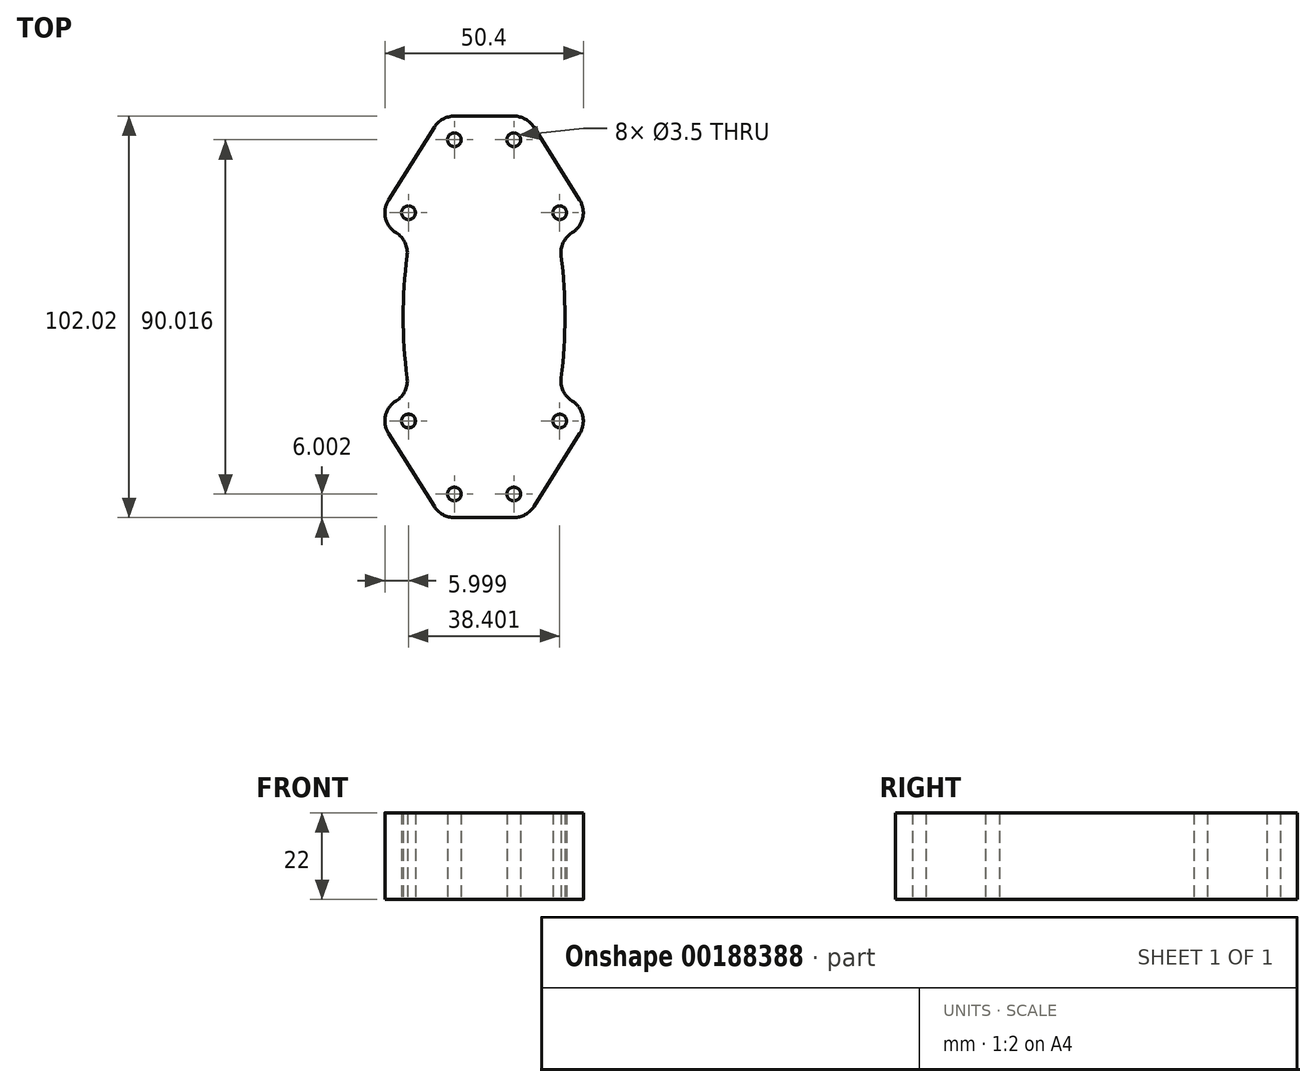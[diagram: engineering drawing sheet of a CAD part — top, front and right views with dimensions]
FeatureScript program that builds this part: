
annotation { "Feature Type Name" : "Feature", "Feature Type Description" : "" }
export const myFeature = defineFeature(function(context is Context, id is Id, definition is map)
    precondition{}
    {
        {
            var Q0;
            Q0=qCreatedBy(makeId("Top.planeOp"),FACE);
            var sketch = newSketch(context, id + "F0", { "sketchPlane" : qUnion([Q0])});
            skLineSegment(sketch, "E0.bottom", {"start": v(18, 18) * mm, "end": v(-18, 18) * mm});
            skLineSegment(sketch, "E0.top", {"start": v(18, -18) * mm, "end": v(-18, -18) * mm});
            skLineSegment(sketch, "E0.left", {"start": v(18, 18) * mm, "end": v(18, -18) * mm});
            skLineSegment(sketch, "E0.right", {"start": v(-18, 18) * mm, "end": v(-18, -18) * mm});
            skPoint(sketch, "E0.middle", {"position": v(0, 0) * mm});
            skLineSegment(sketch, "E1.bottom", {"start": v(15.25, 15.25) * mm, "end": v(-15.25, 15.25) * mm, "construction": true});
            skLineSegment(sketch, "E1.top", {"start": v(15.25, -15.25) * mm, "end": v(-15.25, -15.25) * mm, "construction": true});
            skLineSegment(sketch, "E1.left", {"start": v(15.25, 15.25) * mm, "end": v(15.25, -15.25) * mm, "construction": true});
            skLineSegment(sketch, "E1.right", {"start": v(-15.25, 15.25) * mm, "end": v(-15.25, -15.25) * mm, "construction": true});
            skCircle(sketch, "E2", {"center": v(-15.25, 15.25) * mm, "radius": 1.7 * mm});
            skCircle(sketch, "E3", {"center": v(15.25, 15.25) * mm, "radius": 1.7 * mm});
            skCircle(sketch, "E4", {"center": v(15.25, -15.25) * mm, "radius": 1.7 * mm});
            skCircle(sketch, "E5", {"center": v(-15.25, -15.25) * mm, "radius": 1.7 * mm});
            skLineSegment(sketch, "E6", {"start": v(-73.5, 0) * mm, "end": v(73.5, 0) * mm, "construction": true});
            skLineSegment(sketch, "E7", {"start": v(0, 73.5) * mm, "end": v(0, -73.5) * mm, "construction": true});
            skCircle(sketch, "E8", {"center": v(-73.5, 73.5) * mm, "radius": 63.5 * mm, "construction": true});
            skCircle(sketch, "E9.MirrorC", {"center": v(-73.5, -73.5) * mm, "radius": 63.5 * mm, "construction": true});
            skCircle(sketch, "E10.MirrorC", {"center": v(73.5, 73.5) * mm, "radius": 63.5 * mm, "construction": true});
            skCircle(sketch, "E11.MirrorC", {"center": v(73.5, -73.5) * mm, "radius": 63.5 * mm, "construction": true});
            skLineSegment(sketch, "E12", {"start": v(-73.5, 10) * mm, "end": v(-73.5, -10) * mm, "construction": true});
            skCircle(sketch, "E13", {"center": v(-73.5, -73.5) * mm, "radius": 15 * mm, "construction": true});
            skLineSegment(sketch, "E14.bottom", {"start": v(-56.54, -72.3) * mm, "end": v(-1.5, -37.72) * mm, "construction": true});
            skLineSegment(sketch, "E14.top", {"start": v(-65.05, -58.75) * mm, "end": v(-10.01, -24.17) * mm, "construction": true});
            skLineSegment(sketch, "E14.left", {"start": v(-56.54, -72.3) * mm, "end": v(-65.05, -58.75) * mm, "construction": true});
            skLineSegment(sketch, "E14.right", {"start": v(-1.5, -37.72) * mm, "end": v(-10.01, -24.17) * mm, "construction": true});
            skLineSegment(sketch, "E15", {"start": v(-73.5, -73.5) * mm, "end": v(-5.76, -30.95) * mm, "construction": true});
            skLineSegment(sketch, "E16.MirrorCS", {"start": v(1.5, -37.72) * mm, "end": v(10.01, -24.17) * mm, "construction": true});
            skLineSegment(sketch, "E17.MirrorCS", {"start": v(65.05, -58.75) * mm, "end": v(10.01, -24.17) * mm, "construction": true});
            skCircle(sketch, "E18.MirrorC", {"center": v(73.5, -73.5) * mm, "radius": 15 * mm, "construction": true});
            skLineSegment(sketch, "E19.MirrorCS", {"start": v(56.54, -72.3) * mm, "end": v(65.05, -58.75) * mm, "construction": true});
            skLineSegment(sketch, "E20.MirrorCS", {"start": v(56.54, -72.3) * mm, "end": v(1.5, -37.72) * mm, "construction": true});
            skLineSegment(sketch, "E21.MirrorCS", {"start": v(-1.5, 37.72) * mm, "end": v(-10.01, 24.17) * mm, "construction": true});
            skCircle(sketch, "E22.MirrorC", {"center": v(-73.5, 73.5) * mm, "radius": 15 * mm, "construction": true});
            skLineSegment(sketch, "E23.MirrorCS", {"start": v(-56.54, 72.3) * mm, "end": v(-65.05, 58.75) * mm, "construction": true});
            skLineSegment(sketch, "E24.MirrorCS", {"start": v(-65.05, 58.75) * mm, "end": v(-10.01, 24.17) * mm, "construction": true});
            skLineSegment(sketch, "E25.MirrorCS", {"start": v(-56.54, 72.3) * mm, "end": v(-1.5, 37.72) * mm, "construction": true});
            skCircle(sketch, "E26.MirrorC", {"center": v(73.5, 73.5) * mm, "radius": 15 * mm, "construction": true});
            skLineSegment(sketch, "E27.MirrorCS", {"start": v(56.54, 72.3) * mm, "end": v(65.05, 58.75) * mm, "construction": true});
            skLineSegment(sketch, "E28.MirrorCS", {"start": v(65.05, 58.75) * mm, "end": v(10.01, 24.17) * mm, "construction": true});
            skLineSegment(sketch, "E29.MirrorCS", {"start": v(1.5, 37.72) * mm, "end": v(10.01, 24.17) * mm, "construction": true});
            skLineSegment(sketch, "E30.MirrorCS", {"start": v(56.54, 72.3) * mm, "end": v(1.5, 37.72) * mm, "construction": true});
            skCircle(sketch, "E31", {"center": v(-73.5, -73.5) * mm, "radius": 65 * mm, "construction": true});
            skLineSegment(sketch, "E32.bottom", {"start": v(19.5, 44.5) * mm, "end": v(-19.5, 44.5) * mm, "construction": true});
            skLineSegment(sketch, "E32.top", {"start": v(19.5, -44.5) * mm, "end": v(-19.5, -44.5) * mm, "construction": true});
            skLineSegment(sketch, "E32.left", {"start": v(19.5, 44.5) * mm, "end": v(19.5, -44.5) * mm, "construction": true});
            skLineSegment(sketch, "E32.right", {"start": v(-19.5, 44.5) * mm, "end": v(-19.5, -44.5) * mm, "construction": true});
            skLineSegment(sketch, "E33", {"start": v(5.76, 30.95) * mm, "end": v(60.8, 65.52) * mm, "construction": true});
            skLineSegment(sketch, "E34", {"start": v(-10, -73.5) * mm, "end": v(10, -73.5) * mm, "construction": true});
            skLineSegment(sketch, "E35", {"start": v(-73.5, -73.5) * mm, "end": v(-73.5, 73.5) * mm, "construction": true});
            skLineSegment(sketch, "E36", {"start": v(-73.5, -73.5) * mm, "end": v(73.5, -73.5) * mm, "construction": true});
            skLineSegment(sketch, "E37", {"start": v(18, -18) * mm, "end": v(-18, 18) * mm, "construction": true});
            skCircle(sketch, "E38", {"center": v(73.5, -73.5) * mm, "radius": 65 * mm, "construction": true});
            skCircle(sketch, "E39", {"center": v(73.5, 73.5) * mm, "radius": 65 * mm, "construction": true});
            skCircle(sketch, "E40", {"center": v(-73.5, 73.5) * mm, "radius": 65 * mm, "construction": true});
            skSolve(sketch);
        }
        {
            var Q0;
            Q0=sQuery(id+"F0.wireOp",VERTEX,"E15.end");
            var Q1;
            Q1=sQuery(id+"F0.wireOp",EDGE,"E15");
            cPlane(context, id + "F1", {"entities" : qUnion([Q0, Q1]), "cplaneType" : CPlaneType.LINE_POINT, "offset" : 25 * mm, "width" : 150 * mm, "height" : 150 * mm});
        }
        {
            var Q0;
            Q0=qCreatedBy(makeId("Top.planeOp"),FACE);
            var sketch = newSketch(context, id + "F2", { "sketchPlane" : qUnion([Q0])});
            skLineSegment(sketch, "E41", {"start": v(-24.28, -29.65) * mm, "end": v(-12.63, -48.2) * mm});
            skCircle(sketch, "E42", {"center": v(-7.55, -45) * mm, "radius": 1.75 * mm});
            skCircle(sketch, "E43", {"center": v(-19.2, -26.46) * mm, "radius": 1.75 * mm});
            skCircle(sketch, "E44", {"center": v(-19.2, -26.46) * mm, "radius": 2.95 * mm, "construction": true});
            skCircle(sketch, "E45", {"center": v(-19.2, -26.46) * mm, "radius": 6 * mm, "construction": true});
            skArc(sketch, "E46", {"start": v(-12.63, -48.2) * mm, "mid": v(-10.45, -50.26) * mm, "end": v(-7.55, -51) * mm});
            skArc(sketch, "E47", {"start": v(-24.28, -29.65) * mm, "mid": v(-25.04, -25.1) * mm, "end": v(-22.35, -21.36) * mm});
            skLineSegment(sketch, "E48.0", {"start": v(-73.5, 0) * mm, "end": v(73.5, 0) * mm, "construction": true});
            skArc(sketch, "E49.MirrorCS", {"start": v(-24.28, 29.65) * mm, "mid": v(-25.04, 25.1) * mm, "end": v(-22.35, 21.36) * mm});
            skLineSegment(sketch, "E50.MirrorCS", {"start": v(-24.28, 29.65) * mm, "end": v(-12.63, 48.2) * mm});
            skArc(sketch, "E51.MirrorCS", {"start": v(-12.63, 48.2) * mm, "mid": v(-10.45, 50.26) * mm, "end": v(-7.55, 51) * mm});
            skLineSegment(sketch, "E52.0", {"start": v(0, 73.5) * mm, "end": v(0, -73.5) * mm, "construction": true});
            skArc(sketch, "E53.MirrorCS", {"start": v(24.28, -29.65) * mm, "mid": v(25.04, -25.1) * mm, "end": v(22.35, -21.36) * mm});
            skArc(sketch, "E54.MirrorCS", {"start": v(12.63, 48.2) * mm, "mid": v(10.45, 50.26) * mm, "end": v(7.55, 51) * mm});
            skLineSegment(sketch, "E55.MirrorCS", {"start": v(24.28, 29.65) * mm, "end": v(12.63, 48.2) * mm});
            skArc(sketch, "E56.MirrorCS", {"start": v(24.28, 29.65) * mm, "mid": v(25.04, 25.1) * mm, "end": v(22.35, 21.36) * mm});
            skLineSegment(sketch, "E57.MirrorCS", {"start": v(24.28, -29.65) * mm, "end": v(12.63, -48.2) * mm});
            skArc(sketch, "E58.MirrorCS", {"start": v(12.63, -48.2) * mm, "mid": v(10.45, -50.26) * mm, "end": v(7.55, -51) * mm});
            skLineSegment(sketch, "E59", {"start": v(-7.55, -51) * mm, "end": v(7.55, -51) * mm});
            skLineSegment(sketch, "E60", {"start": v(-7.55, 51) * mm, "end": v(7.55, 51) * mm});
            skCircle(sketch, "E61.MirrorC", {"center": v(7.55, -45) * mm, "radius": 1.75 * mm});
            skCircle(sketch, "E62.MirrorC", {"center": v(19.2, -26.46) * mm, "radius": 1.75 * mm});
            skCircle(sketch, "E63.MirrorC", {"center": v(7.55, 45) * mm, "radius": 1.75 * mm});
            skCircle(sketch, "E64.MirrorC", {"center": v(19.2, 26.46) * mm, "radius": 1.75 * mm});
            skCircle(sketch, "E65.MirrorC", {"center": v(-19.2, 26.46) * mm, "radius": 1.75 * mm});
            skCircle(sketch, "E66.MirrorC", {"center": v(-7.55, 45) * mm, "radius": 1.75 * mm});
            skArc(sketch, "E67", {"start": v(-22.35, -21.36) * mm, "mid": v(-20.08, -18.83) * mm, "end": v(-19.55, -15.48) * mm});
            skArc(sketch, "E68.MirrorCS", {"start": v(-22.35, 21.36) * mm, "mid": v(-20.08, 18.83) * mm, "end": v(-19.55, 15.48) * mm});
            skArc(sketch, "E69.MirrorCS", {"start": v(22.35, -21.36) * mm, "mid": v(20.08, -18.83) * mm, "end": v(19.55, -15.48) * mm});
            skArc(sketch, "E70.MirrorCS", {"start": v(22.35, 21.36) * mm, "mid": v(20.08, 18.83) * mm, "end": v(19.55, 15.48) * mm});
            skArc(sketch, "E71", {"start": v(-19.55, 15.48) * mm, "mid": v(-20.55, 0) * mm, "end": v(-19.55, -15.48) * mm});
            skArc(sketch, "E72.MirrorCS", {"start": v(19.55, 15.48) * mm, "mid": v(20.55, 0) * mm, "end": v(19.55, -15.48) * mm});
            skSolve(sketch);
        }
        {
            var Q0;
            Q0 = qSketchRegion(id + "F2", true);
            extrude(context, id + "F3", {"entities" : qUnion([Q0]), "depth" : 22 * mm, "offsetDistance" : 25 * mm});
        }
    });
